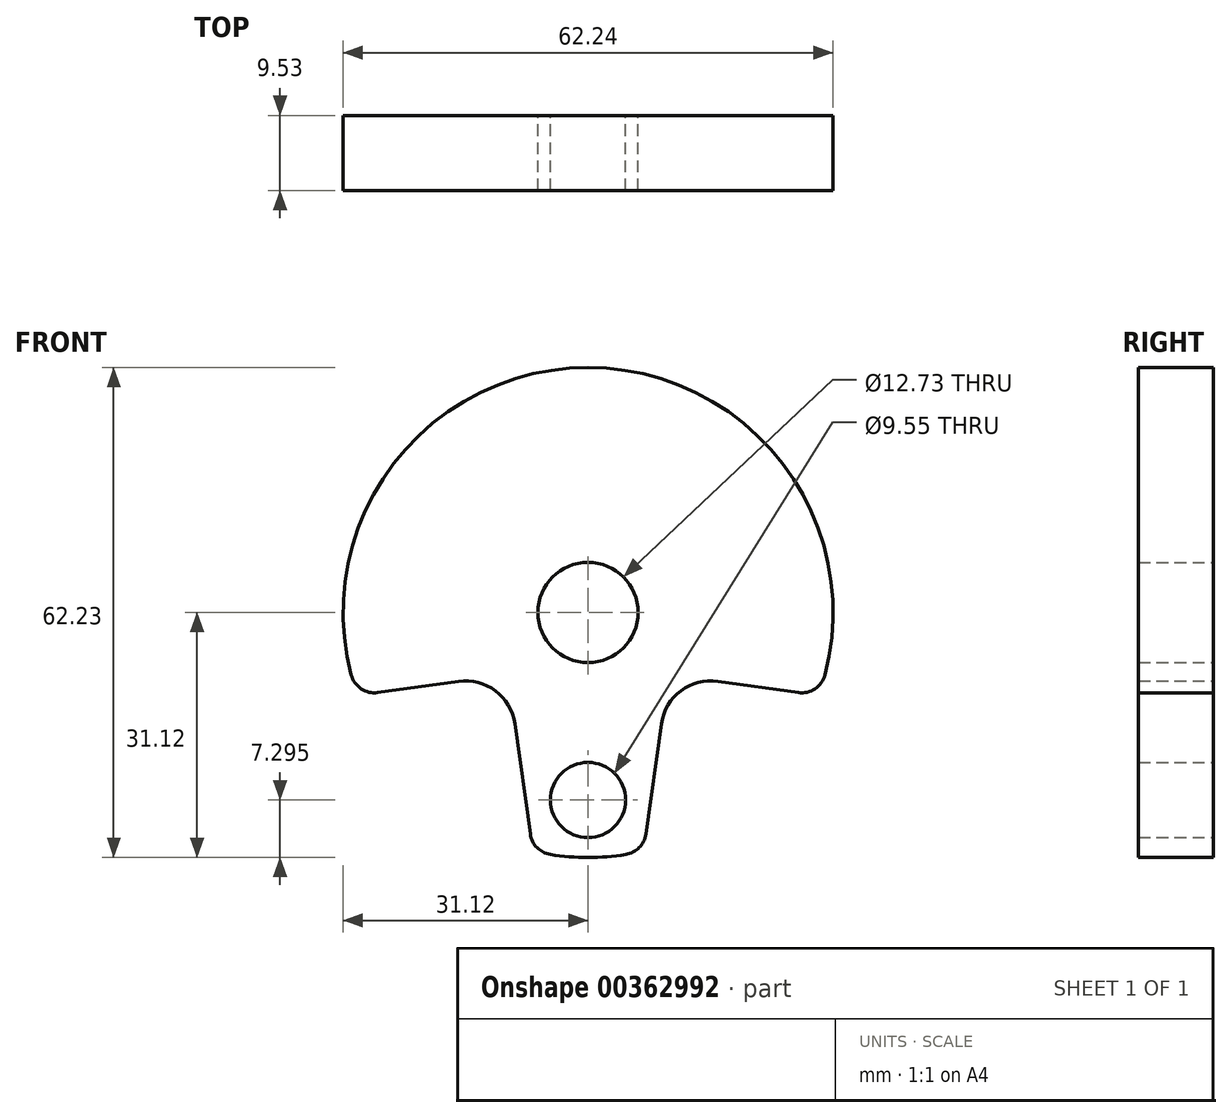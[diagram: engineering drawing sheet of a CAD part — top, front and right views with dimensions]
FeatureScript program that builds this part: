
annotation { "Feature Type Name" : "Feature", "Feature Type Description" : "" }
export const myFeature = defineFeature(function(context is Context, id is Id, definition is map)
    precondition{}
    {
        {
            var Q0;
            Q0=qCreatedBy(makeId("Front.planeOp"),FACE);
            var sketch = newSketch(context, id + "F0", { "sketchPlane" : qUnion([Q0])});
            skArc(sketch, "E0", {"start": v(30.09, -7.94) * mm, "mid": v(0, 31.12) * mm, "end": v(-30.09, -7.94) * mm});
            skCircle(sketch, "E1", {"center": v(0, 0) * mm, "radius": 6.36 * mm});
            skCircle(sketch, "E2", {"center": v(0, -23.83) * mm, "radius": 4.78 * mm});
            skLineSegment(sketch, "E3", {"start": v(-26.71, -10.18) * mm, "end": v(-16.48, -8.74) * mm});
            skLineSegment(sketch, "E4.trimOffspring", {"start": v(0.89, -6.3) * mm, "end": v(1.63, -6.2) * mm});
            skLineSegment(sketch, "E5.trimOffspring", {"start": v(-7.34, -28.16) * mm, "end": v(-9.31, -14.15) * mm});
            skLineSegment(sketch, "E6.MirrorCS", {"start": v(26.71, -10.18) * mm, "end": v(16.48, -8.74) * mm});
            skLineSegment(sketch, "E7.MirrorCS", {"start": v(7.34, -28.16) * mm, "end": v(9.31, -14.15) * mm});
            skArc(sketch, "E8.trimOffspring", {"start": v(-4.8, -30.74) * mm, "mid": v(0, -31.12) * mm, "end": v(4.8, -30.74) * mm});
            skPoint(sketch, "E9.visualSharp", {"position": v(10.2, -7.86) * mm});
            skArc(sketch, "E9.filletArc", {"start": v(16.48, -8.74) * mm, "mid": v(11.78, -9.96) * mm, "end": v(9.31, -14.15) * mm});
            skPoint(sketch, "E10.visualSharp", {"position": v(-10.2, -7.86) * mm});
            skArc(sketch, "E10.filletArc", {"start": v(-9.31, -14.15) * mm, "mid": v(-11.78, -9.96) * mm, "end": v(-16.48, -8.74) * mm});
            skPoint(sketch, "E11.visualSharp", {"position": v(-29.28, -10.54) * mm});
            skArc(sketch, "E11.filletArc", {"start": v(-30.09, -7.94) * mm, "mid": v(-28.83, -9.7) * mm, "end": v(-26.71, -10.18) * mm});
            skPoint(sketch, "E12.visualSharp", {"position": v(29.28, -10.54) * mm});
            skArc(sketch, "E12.filletArc", {"start": v(26.71, -10.18) * mm, "mid": v(28.83, -9.7) * mm, "end": v(30.09, -7.94) * mm});
            skPoint(sketch, "E13.start.orphan", {"position": v(-7.8, -24.92) * mm});
            skPoint(sketch, "E14.trimOffspring.end.orphan", {"position": v(7.8, -24.92) * mm});
            skPoint(sketch, "E15.visualSharp", {"position": v(-7.04, -30.3) * mm});
            skArc(sketch, "E15.filletArc", {"start": v(-7.34, -28.16) * mm, "mid": v(-6.5, -29.87) * mm, "end": v(-4.8, -30.74) * mm});
            skPoint(sketch, "E16.visualSharp", {"position": v(7.04, -30.3) * mm});
            skArc(sketch, "E16.filletArc", {"start": v(4.8, -30.74) * mm, "mid": v(6.5, -29.87) * mm, "end": v(7.34, -28.16) * mm});
            skSolve(sketch);
        }
        {
            var Q0;
            Q0=makeQuery(id+"F0.imprint","IMPRINT",FACE,{"disambiguationData":[TD([[makeQuery(id+"F0.imprint","IMPRINT",EDGE,{"derivedFrom":sQuery(id+"F0.wireOp",EDGE,"E0")}),1.0]])]});
            extrude(context, id + "F1", {"entities" : qUnion([Q0]), "depth" : 9.52 * mm});
        }
    });
